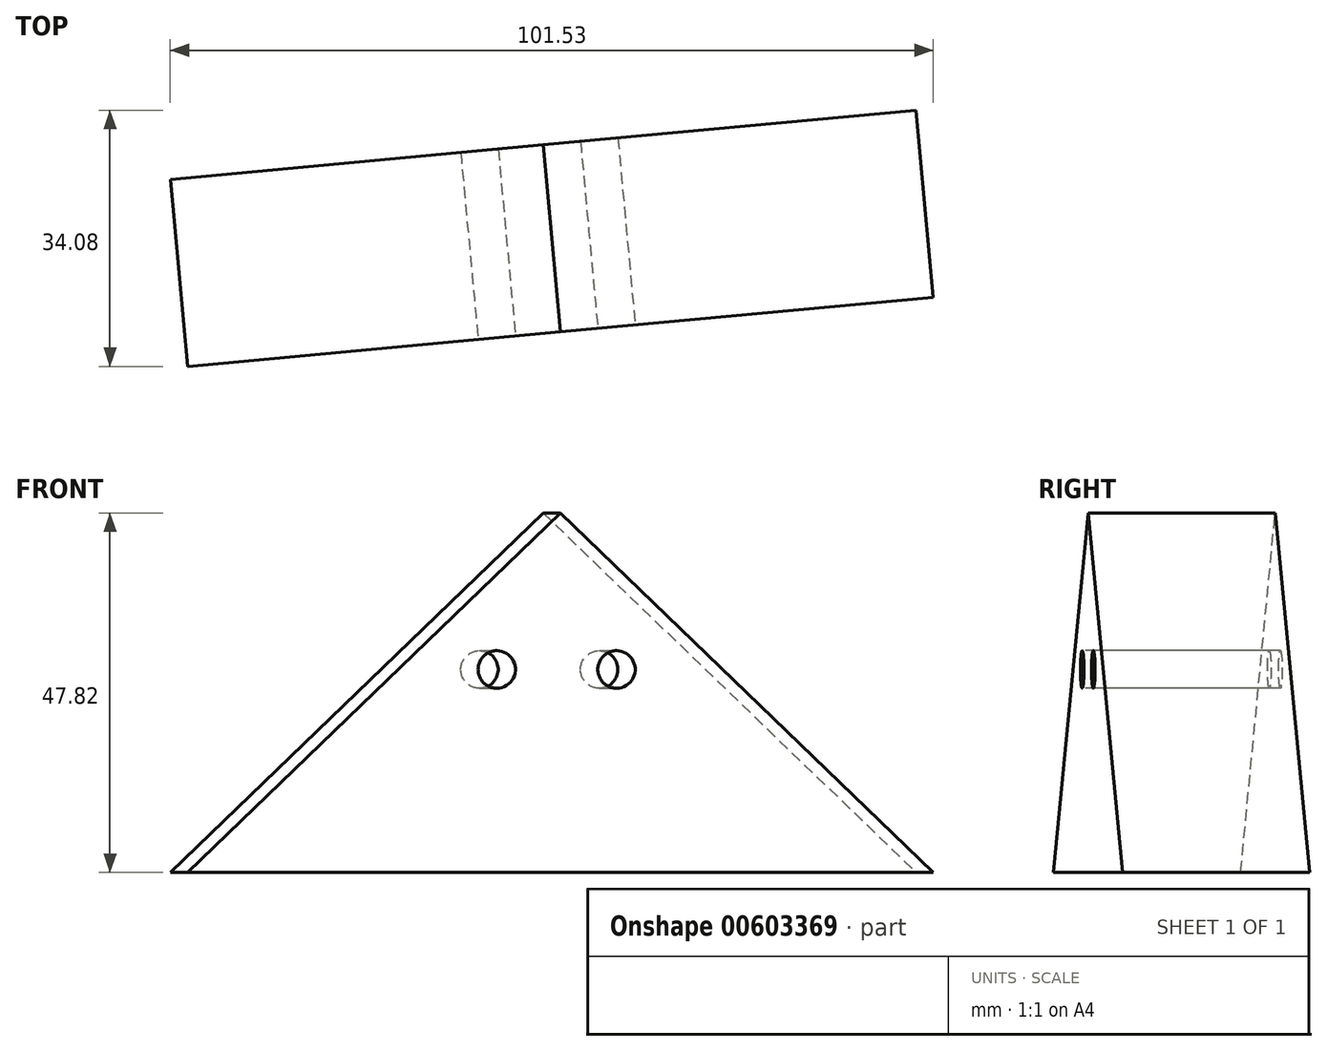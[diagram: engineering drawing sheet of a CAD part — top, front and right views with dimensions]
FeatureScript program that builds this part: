
annotation { "Feature Type Name" : "Feature", "Feature Type Description" : "" }
export const myFeature = defineFeature(function(context is Context, id is Id, definition is map)
    precondition{}
    {
        {
            var Q0;
            Q0=qCreatedBy(makeId("Top.planeOp"),FACE);
            var sketch = newSketch(context, id + "F0", { "sketchPlane" : qUnion([Q0])});
            skLineSegment(sketch, "E0", {"start": v(-327.3, -140.86) * mm, "end": v(-102.6, -140.86) * mm});
            skLineSegment(sketch, "E1", {"start": v(-102.6, -140.86) * mm, "end": v(-102.6, -170.86) * mm});
            skLineSegment(sketch, "E2", {"start": v(-102.6, -170.86) * mm, "end": v(0, -170.86) * mm});
            skLineSegment(sketch, "E3", {"start": v(0, -170.86) * mm, "end": v(0, -140.86) * mm});
            skLineSegment(sketch, "E4", {"start": v(0, -140.86) * mm, "end": v(288.9, -140.86) * mm});
            skLineSegment(sketch, "E5", {"start": v(288.9, -140.86) * mm, "end": v(288.9, 108.14) * mm});
            skLineSegment(sketch, "E6", {"start": v(288.9, 108.14) * mm, "end": v(0, 108.14) * mm});
            skLineSegment(sketch, "E7", {"start": v(0, 108.14) * mm, "end": v(0, 138.14) * mm});
            skLineSegment(sketch, "E8", {"start": v(-102.6, 128.64) * mm, "end": v(-102.6, 108.14) * mm});
            skLineSegment(sketch, "E9", {"start": v(-102.6, 108.14) * mm, "end": v(-327.3, 108.14) * mm});
            skLineSegment(sketch, "E10", {"start": v(-327.3, 108.14) * mm, "end": v(-327.3, -140.86) * mm});
            skLineSegment(sketch, "E11", {"start": v(-102.6, 128.64) * mm, "end": v(0, 138.14) * mm});
            skSolve(sketch);
        }
        {
            var Q0;
            Q0=makeQuery(id+"F0.imprint","IMPRINT",FACE,{"disambiguationData":[TD([[makeQuery(id+"F0.imprint","IMPRINT",EDGE,{"derivedFrom":sQuery(id+"F0.wireOp",EDGE,"E0")}),1.0]])]});
            extrude(context, id + "F1", {"entities" : qUnion([Q0]), "depth" : 8 * mm, "offsetDistance" : 25 * mm});
        }
        {
            var Q0;
            Q0=makeQuery(id+"F1.opExtrude","SWEPT_FACE",FACE,{"disambiguationData":[OSD([sQuery(id+"F0.wireOp",EDGE,"E5")])]});
            var sketch = newSketch(context, id + "F2", { "sketchPlane" : qUnion([Q0])});
            skLineSegment(sketch, "E12", {"start": v(-146.36, 8) * mm, "end": v(113.64, 8) * mm});
            skPoint(sketch, "E13", {"position": v(-140.86, 8) * mm});
            skPoint(sketch, "E14", {"position": v(108.14, 8) * mm});
            skLineSegment(sketch, "E15", {"start": v(-146.36, 8) * mm, "end": v(-16.36, 51.45) * mm});
            skLineSegment(sketch, "E16", {"start": v(-16.36, 51.45) * mm, "end": v(113.64, 8) * mm});
            skPoint(sketch, "E17", {"position": v(-16.36, 8) * mm});
            skSolve(sketch);
        }
        {
            var Q0;
            {var subQ0=sQuery(id+"F2.wireOp",EDGE,"E15");Q0=makeQuery(id+"F2.imprint","IMPRINT",FACE,{"disambiguationData":[TD([[makeQuery(id+"F2.imprint","IMPRINT",EDGE,{"derivedFrom":subQ0}),-1.0]])]});}
            extrude(context, id + "F3", {"entities" : qUnion([Q0]), "operationType" : NewBodyOperationType.ADD, "oppositeDirection" : true, "depth" : (616.2 + 5.5) * mm, "offsetDistance" : 25 * mm});
        }
        {
            var Q0;
            Q0=qSketchRegion(id+"F2",true);
            extrude(context, id + "F4", {"entities" : qUnion([Q0]), "operationType" : NewBodyOperationType.ADD, "depth" : 5.5 * mm, "offsetDistance" : 25 * mm});
        }
        {
            var Q0;
            Q0=makeQuery(id+"F1.opExtrude","SWEPT_FACE",FACE,{"disambiguationData":[OSD([sQuery(id+"F0.wireOp",EDGE,"E2")])]});
            var sketch = newSketch(context, id + "F5", { "sketchPlane" : qUnion([Q0])});
            skLineSegment(sketch, "E18", {"start": v(-108.1, 8) * mm, "end": v(5.5, 8) * mm});
            skPoint(sketch, "E19", {"position": v(-102.6, 8) * mm});
            skPoint(sketch, "E20", {"position": v(0, 8) * mm});
            skPoint(sketch, "E21", {"position": v(-51.3, 8) * mm});
            skLineSegment(sketch, "E22", {"start": v(-51.3, 8) * mm, "end": v(-51.3, 90.85) * mm, "construction": true});
            skPoint(sketch, "E23", {"position": v(-51.3, 62.75) * mm});
            skLineSegment(sketch, "E24", {"start": v(-108.1, 8) * mm, "end": v(-51.3, 62.75) * mm});
            skLineSegment(sketch, "E25", {"start": v(-51.3, 62.75) * mm, "end": v(5.5, 8) * mm});
            skSolve(sketch);
        }
        {
            var Q0;
            Q0=qSketchRegion(id+"F5",true);
            var Q1;
            Q1=makeQuery(id+"F1.opExtrude","SWEPT_FACE",FACE,{"disambiguationData":[OSD([sQuery(id+"F0.wireOp",EDGE,"E11")])]});
            extrude(context, id + "F6", {"entities" : qUnion([Q0]), "operationType" : NewBodyOperationType.ADD, "endBound" : BoundingType.UP_TO_SURFACE, "oppositeDirection" : true, "depth" : 25 * mm, "endBoundEntityFace" : qUnion([Q1]), "hasOffset" : true, "offsetDistance" : -5.5 * mm});
        }
        {
            var Q0;
            Q0=qSketchRegion(id+"F5",true);
            extrude(context, id + "F7", {"entities" : qUnion([Q0]), "operationType" : NewBodyOperationType.ADD, "depth" : 5.5 * mm, "offsetDistance" : 25 * mm});
        }
        {
            var Q0;
            Q0=makeQuery(id+"F6.opExtrude","CAP_FACE",FACE,{"disambiguationData":[OSD([sQuery(id+"F5.wireOp",EDGE,"E18"),sQuery(id+"F5.wireOp",EDGE,"E24"),sQuery(id+"F5.wireOp",EDGE,"E25")])],"isStart":false});
            var sketch = newSketch(context, id + "F8", { "sketchPlane" : qUnion([Q0])});
            skLineSegment(sketch, "E26.0", {"start": v(38.28, 55.82) * mm, "end": v(-15.3, 4.4) * mm});
            skLineSegment(sketch, "E26.1", {"start": v(91.86, 4.4) * mm, "end": v(38.28, 55.82) * mm});
            skLineSegment(sketch, "E27", {"start": v(-15.3, 4.4) * mm, "end": v(91.86, 4.4) * mm});
            skSolve(sketch);
        }
        {
            var Q0;
            {var subQ0=sQuery(id+"F8.wireOp",EDGE,"E26.1");var subQ1=sQuery(id+"F8.wireOp",EDGE,"E26.0");var subQ2=makeQuery(id+"F8.imprint","INTERSECT",VERTEX,{"derivedFrom":[subQ1,subQ0]});Q0=makeQuery(id+"F8.imprint","IMPRINT",FACE,{"disambiguationData":[TD([[makeQuery(id+"F8.imprint","IMPRINT",EDGE,{"disambiguationData":[TD([[subQ2,-1.0]])],"derivedFrom":subQ1}),1.0]])]});}
            extrude(context, id + "F9", {"entities" : qUnion([Q0]), "operationType" : NewBodyOperationType.REMOVE, "oppositeDirection" : true, "depth" : 5.5 * mm, "offsetDistance" : 25 * mm});
        }
        {
            var Q0;
            Q0=makeQuery(id+"F3.opExtrude","CAP_FACE",FACE,{"disambiguationData":[OSD([sQuery(id+"F2.wireOp",EDGE,"E12"),sQuery(id+"F2.wireOp",EDGE,"E15"),sQuery(id+"F2.wireOp",EDGE,"E16")])],"isStart":false});
            var sketch = newSketch(context, id + "F10", { "sketchPlane" : qUnion([Q0])});
            skLineSegment(sketch, "E28.0", {"start": v(16.36, 45.65) * mm, "end": v(-111.9, 2.78) * mm});
            skLineSegment(sketch, "E28.1", {"start": v(144.61, 2.78) * mm, "end": v(16.36, 45.65) * mm});
            skLineSegment(sketch, "E29", {"start": v(-111.9, 2.78) * mm, "end": v(144.61, 2.78) * mm});
            skSolve(sketch);
        }
        {
            var Q0;
            Q0=qSketchRegion(id+"F10",true);
            extrude(context, id + "F11", {"entities" : qUnion([Q0]), "operationType" : NewBodyOperationType.REMOVE, "oppositeDirection" : true, "depth" : 5.5 * mm, "offsetDistance" : 25 * mm});
        }
        {
            var Q0;
            Q0=makeQuery(id+"F4.opExtrude","CAP_FACE",FACE,{"disambiguationData":[OSD([sQuery(id+"F2.wireOp",EDGE,"E12"),sQuery(id+"F2.wireOp",EDGE,"E15"),sQuery(id+"F2.wireOp",EDGE,"E16")])],"isStart":false});
            var sketch = newSketch(context, id + "F12", { "sketchPlane" : qUnion([Q0])});
            skLineSegment(sketch, "E30.0", {"start": v(-16.36, 45.65) * mm, "end": v(111.9, 2.78) * mm});
            skLineSegment(sketch, "E30.1", {"start": v(-144.61, 2.78) * mm, "end": v(-16.36, 45.65) * mm});
            skLineSegment(sketch, "E31", {"start": v(-144.61, 2.78) * mm, "end": v(111.9, 2.78) * mm});
            skSolve(sketch);
        }
        {
            var Q0;
            Q0=qSketchRegion(id+"F12",true);
            extrude(context, id + "F13", {"entities" : qUnion([Q0]), "operationType" : NewBodyOperationType.REMOVE, "oppositeDirection" : true, "depth" : 5.5 * mm, "offsetDistance" : 25 * mm});
        }
        {
            var Q0;
            Q0=makeQuery(id+"F7.opExtrude","CAP_FACE",FACE,{"disambiguationData":[OSD([sQuery(id+"F5.wireOp",EDGE,"E18"),sQuery(id+"F5.wireOp",EDGE,"E24"),sQuery(id+"F5.wireOp",EDGE,"E25")])],"isStart":false});
            var sketch = newSketch(context, id + "F14", { "sketchPlane" : qUnion([Q0])});
            skLineSegment(sketch, "E32.0", {"start": v(-51.3, 55.11) * mm, "end": v(1.68, 4.04) * mm});
            skLineSegment(sketch, "E32.1", {"start": v(-104.28, 4.04) * mm, "end": v(-51.3, 55.11) * mm});
            skLineSegment(sketch, "E33", {"start": v(-104.28, 4.04) * mm, "end": v(1.68, 4.04) * mm});
            skSolve(sketch);
        }
        {
            var Q0;
            Q0=qSketchRegion(id+"F14",true);
            extrude(context, id + "F15", {"entities" : qUnion([Q0]), "operationType" : NewBodyOperationType.REMOVE, "oppositeDirection" : true, "depth" : 5.5 * mm, "offsetDistance" : 25 * mm});
        }
        {
            var Q0;
            Q0=makeQuery(id+"F4.opExtrude","CAP_FACE",FACE,{"disambiguationData":[OSD([sQuery(id+"F2.wireOp",EDGE,"E12"),sQuery(id+"F2.wireOp",EDGE,"E15"),sQuery(id+"F2.wireOp",EDGE,"E16")])],"isStart":false});
            var sketch = newSketch(context, id + "F16", { "sketchPlane" : qUnion([Q0])});
            skLineSegment(sketch, "E34", {"start": v(-36.64, 44.67) * mm, "end": v(-16.36, 51.45) * mm});
            skLineSegment(sketch, "E35", {"start": v(-16.36, 51.45) * mm, "end": v(3.93, 44.67) * mm});
            skLineSegment(sketch, "E36.0", {"start": v(-16.36, 55.67) * mm, "end": v(5.2, 48.47) * mm});
            skLineSegment(sketch, "E36.1", {"start": v(-37.91, 48.47) * mm, "end": v(-16.36, 55.67) * mm});
            skLineSegment(sketch, "E37", {"start": v(-37.91, 48.47) * mm, "end": v(-36.64, 44.67) * mm});
            skLineSegment(sketch, "E38", {"start": v(5.2, 48.47) * mm, "end": v(3.93, 44.67) * mm});
            skSolve(sketch);
        }
        {
            var Q0;
            Q0=makeQuery(id+"F16.imprint","IMPRINT",FACE,{"disambiguationData":[TD([[makeQuery(id+"F16.imprint","IMPRINT",EDGE,{"derivedFrom":sQuery(id+"F16.wireOp",EDGE,"E34")}),1.0]])]});
            extrude(context, id + "F17", {"entities" : qUnion([Q0]), "operationType" : NewBodyOperationType.ADD, "oppositeDirection" : true, "depth" : (30.35 + 277.85) * mm, "offsetDistance" : 25 * mm});
        }
        {
            var Q0;
            Q0=qSketchRegion(id+"F16",true);
            extrude(context, id + "F18", {"entities" : qUnion([Q0]), "operationType" : NewBodyOperationType.REMOVE, "oppositeDirection" : true, "depth" : 24 * mm, "offsetDistance" : 25 * mm});
        }
        {
            var Q0;
            Q0=makeQuery(id+"F3.opExtrude","CAP_FACE",FACE,{"disambiguationData":[OSD([sQuery(id+"F2.wireOp",EDGE,"E12"),sQuery(id+"F2.wireOp",EDGE,"E15"),sQuery(id+"F2.wireOp",EDGE,"E16")])],"isStart":false});
            var sketch = newSketch(context, id + "F19", { "sketchPlane" : qUnion([Q0])});
            skLineSegment(sketch, "E39", {"start": v(-3.93, 44.67) * mm, "end": v(16.36, 51.45) * mm});
            skLineSegment(sketch, "E40", {"start": v(16.36, 51.45) * mm, "end": v(36.64, 44.67) * mm});
            skLineSegment(sketch, "E41.0", {"start": v(16.36, 55.67) * mm, "end": v(37.91, 48.47) * mm});
            skLineSegment(sketch, "E41.1", {"start": v(-5.2, 48.47) * mm, "end": v(16.36, 55.67) * mm});
            skLineSegment(sketch, "E42", {"start": v(-5.2, 48.47) * mm, "end": v(-3.93, 44.67) * mm});
            skLineSegment(sketch, "E43", {"start": v(37.91, 48.47) * mm, "end": v(36.64, 44.67) * mm});
            skSolve(sketch);
        }
        {
            var Q0;
            Q0=qSketchRegion(id+"F19",true);
            extrude(context, id + "F20", {"entities" : qUnion([Q0]), "operationType" : NewBodyOperationType.ADD, "oppositeDirection" : true, "depth" : (30.35 + 213.85) * mm, "offsetDistance" : 25 * mm});
        }
        {
            var Q0;
            Q0=qSketchRegion(id+"F19",true);
            extrude(context, id + "F21", {"entities" : qUnion([Q0]), "operationType" : NewBodyOperationType.REMOVE, "oppositeDirection" : true, "depth" : 30.35 * mm, "offsetDistance" : 25 * mm});
        }
        {
            var Q0;
            Q0=makeQuery(id+"F11.boolean.opBoolean","MERGE",FACE,{"derivedFrom":[makeQuery(id+"F1.opExtrude","SWEPT_FACE",FACE,{"disambiguationData":[OSD([sQuery(id+"F0.wireOp",EDGE,"E10")])]}),makeQuery(id+"F11.opExtrude","CAP_FACE",FACE,{"disambiguationData":[OSD([sQuery(id+"F10.wireOp",EDGE,"E28.0"),sQuery(id+"F10.wireOp",EDGE,"E28.1"),sQuery(id+"F10.wireOp",EDGE,"E29")])],"isStart":false})]});
            var sketch = newSketch(context, id + "F22", { "sketchPlane" : qUnion([Q0])});
            skPoint(sketch, "E44", {"position": v(16.36, 0) * mm});
            skLineSegment(sketch, "E45", {"start": v(16.36, 0) * mm, "end": v(16.36, 35) * mm, "construction": true});
            skLineSegment(sketch, "E46", {"start": v(-4.2, 35) * mm, "end": v(35.76, 35) * mm, "construction": true});
            skPoint(sketch, "E47", {"position": v(8.36, 35) * mm});
            skPoint(sketch, "E48", {"position": v(24.36, 35) * mm});
            skCircle(sketch, "E49", {"center": v(8.36, 35) * mm, "radius": 2.5 * mm});
            skCircle(sketch, "E50", {"center": v(24.36, 35) * mm, "radius": 2.5 * mm});
            skSolve(sketch);
        }
        {
            var Q0;
            Q0=qSketchRegion(id+"F22",true);
            extrude(context, id + "F23", {"entities" : qUnion([Q0]), "operationType" : NewBodyOperationType.REMOVE, "oppositeDirection" : true, "depth" : .5 * mm, "offsetDistance" : 25 * mm});
        }
        {
            var Q0;
            Q0=makeQuery(id+"F13.boolean.opBoolean","MERGE",FACE,{"derivedFrom":[makeQuery(id+"F3.boolean.opBoolean","MERGE",FACE,{"derivedFrom":[makeQuery(id+"F1.opExtrude","SWEPT_FACE",FACE,{"disambiguationData":[OSD([sQuery(id+"F0.wireOp",EDGE,"E5")])]}),makeQuery(id+"F3.opExtrude","CAP_FACE",FACE,{"disambiguationData":[OSD([sQuery(id+"F2.wireOp",EDGE,"E12"),sQuery(id+"F2.wireOp",EDGE,"E15"),sQuery(id+"F2.wireOp",EDGE,"E16")])],"isStart":true})]}),makeQuery(id+"F13.opExtrude","CAP_FACE",FACE,{"disambiguationData":[OSD([sQuery(id+"F12.wireOp",EDGE,"E30.0"),sQuery(id+"F12.wireOp",EDGE,"E30.1"),sQuery(id+"F12.wireOp",EDGE,"E31")])],"isStart":false})]});
            var sketch = newSketch(context, id + "F24", { "sketchPlane" : qUnion([Q0])});
            skPoint(sketch, "E51", {"position": v(-16.36, 0) * mm});
            skLineSegment(sketch, "E52", {"start": v(-16.36, 0) * mm, "end": v(-16.36, 35) * mm, "construction": true});
            skLineSegment(sketch, "E53", {"start": v(-48.45, 35) * mm, "end": v(-8.49, 35) * mm, "construction": true});
            skPoint(sketch, "E54", {"position": v(-24.36, 35) * mm});
            skPoint(sketch, "E55", {"position": v(-8.36, 35) * mm});
            skCircle(sketch, "E56", {"center": v(-24.36, 35) * mm, "radius": 2.5 * mm});
            skCircle(sketch, "E57", {"center": v(-8.36, 35) * mm, "radius": 2.5 * mm});
            skSolve(sketch);
        }
        {
            var Q0;
            Q0=qSketchRegion(id+"F24",true);
            extrude(context, id + "F25", {"entities" : qUnion([Q0]), "operationType" : NewBodyOperationType.REMOVE, "oppositeDirection" : true, "depth" : .5 * mm, "offsetDistance" : 25 * mm});
        }
        {
            var Q0;
            Q0=makeQuery(id+"F15.boolean.opBoolean","MERGE",FACE,{"derivedFrom":[makeQuery(id+"F6.boolean.opBoolean","MERGE",FACE,{"derivedFrom":[makeQuery(id+"F1.opExtrude","SWEPT_FACE",FACE,{"disambiguationData":[OSD([sQuery(id+"F0.wireOp",EDGE,"E2")])]}),makeQuery(id+"F6.opExtrude","CAP_FACE",FACE,{"disambiguationData":[OSD([sQuery(id+"F5.wireOp",EDGE,"E18"),sQuery(id+"F5.wireOp",EDGE,"E24"),sQuery(id+"F5.wireOp",EDGE,"E25")])],"isStart":true})]})],"fromTools":[makeQuery(id+"F15.opExtrude","CAP_FACE",FACE,{"disambiguationData":[OSD([sQuery(id+"F14.wireOp",EDGE,"E32.0"),sQuery(id+"F14.wireOp",EDGE,"E32.1"),sQuery(id+"F14.wireOp",EDGE,"E33")])],"isStart":false})]});
            var sketch = newSketch(context, id + "F26", { "sketchPlane" : qUnion([Q0])});
            skPoint(sketch, "E58", {"position": v(-51.3, 0) * mm});
            skLineSegment(sketch, "E59", {"start": v(-51.3, 0) * mm, "end": v(-51.3, 35) * mm, "construction": true});
            skLineSegment(sketch, "E60", {"start": v(-73.66, 35) * mm, "end": v(-33.7, 35) * mm, "construction": true});
            skPoint(sketch, "E61", {"position": v(-59.3, 35) * mm});
            skPoint(sketch, "E62", {"position": v(-43.3, 35) * mm});
            skCircle(sketch, "E63", {"center": v(-59.3, 35) * mm, "radius": 2.5 * mm});
            skCircle(sketch, "E64", {"center": v(-43.3, 35) * mm, "radius": 2.5 * mm});
            skSolve(sketch);
        }
        {
            var Q0;
            Q0=qSketchRegion(id+"F26",true);
            extrude(context, id + "F27", {"entities" : qUnion([Q0]), "operationType" : NewBodyOperationType.REMOVE, "oppositeDirection" : true, "depth" : .5 * mm, "offsetDistance" : 25 * mm});
        }
        {
            var Q0;
            Q0=makeQuery(id+"F1.opExtrude","SWEPT_FACE",FACE,{"disambiguationData":[OSD([sQuery(id+"F0.wireOp",EDGE,"E11")])]});
            var sketch = newSketch(context, id + "F28", { "sketchPlane" : qUnion([Q0])});
            skPoint(sketch, "E65", {"position": v(38.78, 0) * mm});
            skLineSegment(sketch, "E66", {"start": v(38.78, 0) * mm, "end": v(38.78, 35) * mm, "construction": true});
            skLineSegment(sketch, "E67", {"start": v(13.04, 35) * mm, "end": v(53, 35) * mm, "construction": true});
            skPoint(sketch, "E68", {"position": v(30.78, 35) * mm});
            skPoint(sketch, "E69", {"position": v(46.78, 35) * mm});
            skCircle(sketch, "E70", {"center": v(30.78, 35) * mm, "radius": 2.5 * mm});
            skCircle(sketch, "E71", {"center": v(46.78, 35) * mm, "radius": 2.5 * mm});
            skSolve(sketch);
        }
        {
            var Q0;
            Q0=qSketchRegion(id+"F28",true);
            extrude(context, id + "F29", {"entities" : qUnion([Q0]), "operationType" : NewBodyOperationType.REMOVE, "oppositeDirection" : true, "depth" : .5 * mm, "offsetDistance" : 25 * mm});
        }
        {
            var Q0;
            Q0=makeQuery(id+"F13.boolean.opBoolean","MERGE",FACE,{"derivedFrom":[makeQuery(id+"F3.boolean.opBoolean","MERGE",FACE,{"derivedFrom":[makeQuery(id+"F1.opExtrude","SWEPT_FACE",FACE,{"disambiguationData":[OSD([sQuery(id+"F0.wireOp",EDGE,"E5")])]}),makeQuery(id+"F3.opExtrude","CAP_FACE",FACE,{"disambiguationData":[OSD([sQuery(id+"F2.wireOp",EDGE,"E12"),sQuery(id+"F2.wireOp",EDGE,"E15"),sQuery(id+"F2.wireOp",EDGE,"E16")])],"isStart":true})]}),makeQuery(id+"F13.opExtrude","CAP_FACE",FACE,{"disambiguationData":[OSD([sQuery(id+"F12.wireOp",EDGE,"E30.0"),sQuery(id+"F12.wireOp",EDGE,"E30.1"),sQuery(id+"F12.wireOp",EDGE,"E31")])],"isStart":false})]});
            var sketch = newSketch(context, id + "F30", { "sketchPlane" : qUnion([Q0])});
            skPoint(sketch, "E72", {"position": v(-16.36, 0) * mm});
            skLineSegment(sketch, "E73", {"start": v(-16.36, 0) * mm, "end": v(-16.36, 40.85) * mm, "construction": true});
            skLineSegment(sketch, "E74.bottom", {"start": v(-23.43, 23) * mm, "end": v(-9.29, 23) * mm});
            skLineSegment(sketch, "E74.top", {"start": v(-23.43, 5) * mm, "end": v(-9.29, 5) * mm});
            skLineSegment(sketch, "E74.left", {"start": v(-23.43, 23) * mm, "end": v(-23.43, 5) * mm});
            skLineSegment(sketch, "E74.right", {"start": v(-9.29, 23) * mm, "end": v(-9.29, 5) * mm});
            skLineSegment(sketch, "E75.0", {"start": v(-21.5, 21.07) * mm, "end": v(-17.32, 21.07) * mm});
            skLineSegment(sketch, "E75.1", {"start": v(-21.5, 21.07) * mm, "end": v(-21.5, 14.96) * mm});
            skLineSegment(sketch, "E75.2", {"start": v(-21.5, 6.93) * mm, "end": v(-17.32, 6.93) * mm});
            skLineSegment(sketch, "E75.3", {"start": v(-11.21, 21.07) * mm, "end": v(-11.21, 14.96) * mm});
            skLineSegment(sketch, "E76.left", {"start": v(-17.32, 21.07) * mm, "end": v(-17.32, 14.96) * mm});
            skLineSegment(sketch, "E76.right", {"start": v(-15.4, 21.07) * mm, "end": v(-15.4, 14.96) * mm});
            skLineSegment(sketch, "E77.bottom", {"start": v(-11.21, 14.96) * mm, "end": v(-15.4, 14.96) * mm});
            skLineSegment(sketch, "E77.top", {"start": v(-11.21, 13.04) * mm, "end": v(-15.4, 13.04) * mm});
            skLineSegment(sketch, "E78.trimOffspring", {"start": v(-17.32, 14.96) * mm, "end": v(-21.5, 14.96) * mm});
            skLineSegment(sketch, "E79.trimOffspring", {"start": v(-17.32, 13.04) * mm, "end": v(-17.32, 6.93) * mm});
            skLineSegment(sketch, "E80.trimOffspring", {"start": v(-17.32, 13.04) * mm, "end": v(-21.5, 13.04) * mm});
            skLineSegment(sketch, "E81.trimOffspring", {"start": v(-15.4, 13.04) * mm, "end": v(-15.4, 6.93) * mm});
            skLineSegment(sketch, "E82.trimOffspring", {"start": v(-11.21, 13.04) * mm, "end": v(-11.21, 6.93) * mm});
            skLineSegment(sketch, "E83.trimOffspring", {"start": v(-21.5, 13.04) * mm, "end": v(-21.5, 6.93) * mm});
            skLineSegment(sketch, "E84.trimOffspring", {"start": v(-15.4, 21.07) * mm, "end": v(-11.21, 21.07) * mm});
            skLineSegment(sketch, "E85.trimOffspring", {"start": v(-15.4, 6.93) * mm, "end": v(-11.21, 6.93) * mm});
            skPoint(sketch, "E86", {"position": v(-16.36, 23) * mm});
            skLineSegment(sketch, "E87.1.0.0", {"start": v(19.6, 13.04) * mm, "end": v(19.6, 6.93) * mm});
            skPoint(sketch, "E87.1.0.1", {"position": v(18.64, 23) * mm});
            skLineSegment(sketch, "E87.1.0.2", {"start": v(19.6, 6.93) * mm, "end": v(23.79, 6.93) * mm});
            skLineSegment(sketch, "E87.1.0.3", {"start": v(13.5, 13.04) * mm, "end": v(13.5, 6.93) * mm});
            skLineSegment(sketch, "E87.1.0.4", {"start": v(17.68, 13.04) * mm, "end": v(17.68, 6.93) * mm});
            skLineSegment(sketch, "E87.1.0.5", {"start": v(11.57, 5) * mm, "end": v(25.71, 5) * mm});
            skLineSegment(sketch, "E87.1.0.6", {"start": v(11.57, 23) * mm, "end": v(25.71, 23) * mm});
            skLineSegment(sketch, "E87.1.0.7", {"start": v(25.71, 23) * mm, "end": v(25.71, 5) * mm});
            skLineSegment(sketch, "E87.1.0.8", {"start": v(11.57, 23) * mm, "end": v(11.57, 5) * mm});
            skLineSegment(sketch, "E87.1.0.9", {"start": v(23.79, 13.04) * mm, "end": v(23.79, 6.93) * mm});
            skLineSegment(sketch, "E87.1.0.10", {"start": v(23.79, 13.04) * mm, "end": v(19.6, 13.04) * mm});
            skLineSegment(sketch, "E87.1.0.11", {"start": v(17.68, 21.07) * mm, "end": v(17.68, 14.96) * mm});
            skLineSegment(sketch, "E87.1.0.12", {"start": v(13.5, 21.07) * mm, "end": v(17.68, 21.07) * mm});
            skLineSegment(sketch, "E87.1.0.13", {"start": v(19.6, 21.07) * mm, "end": v(19.6, 14.96) * mm});
            skLineSegment(sketch, "E87.1.0.14", {"start": v(13.5, 6.93) * mm, "end": v(17.68, 6.93) * mm});
            skLineSegment(sketch, "E87.1.0.15", {"start": v(23.79, 21.07) * mm, "end": v(23.79, 14.96) * mm});
            skLineSegment(sketch, "E87.1.0.16", {"start": v(17.68, 13.04) * mm, "end": v(13.5, 13.04) * mm});
            skLineSegment(sketch, "E87.1.0.17", {"start": v(17.68, 14.96) * mm, "end": v(13.5, 14.96) * mm});
            skLineSegment(sketch, "E87.1.0.18", {"start": v(23.79, 14.96) * mm, "end": v(19.6, 14.96) * mm});
            skLineSegment(sketch, "E87.1.0.19", {"start": v(19.6, 21.07) * mm, "end": v(23.79, 21.07) * mm});
            skLineSegment(sketch, "E87.1.0.20", {"start": v(13.5, 21.07) * mm, "end": v(13.5, 14.96) * mm});
            skLineSegment(sketch, "E87.direction1", {"start": v(-23.43, 5) * mm, "end": v(11.57, 5) * mm, "construction": true});
            skLineSegment(sketch, "E88.1.0.0", {"start": v(-50.4, 6.93) * mm, "end": v(-46.21, 6.93) * mm});
            skPoint(sketch, "E88.1.0.1", {"position": v(-51.36, 0) * mm});
            skLineSegment(sketch, "E88.1.0.2", {"start": v(-58.43, 5) * mm, "end": v(-44.29, 5) * mm});
            skLineSegment(sketch, "E88.1.0.3", {"start": v(-44.29, 23) * mm, "end": v(-44.29, 5) * mm});
            skLineSegment(sketch, "E88.1.0.4", {"start": v(-58.43, 23) * mm, "end": v(-58.43, 5) * mm});
            skLineSegment(sketch, "E88.1.0.5", {"start": v(-46.21, 21.07) * mm, "end": v(-46.21, 14.96) * mm});
            skLineSegment(sketch, "E88.1.0.6", {"start": v(-56.5, 6.93) * mm, "end": v(-52.32, 6.93) * mm});
            skPoint(sketch, "E88.1.0.7", {"position": v(-51.36, 23) * mm});
            skLineSegment(sketch, "E88.1.0.8", {"start": v(-50.4, 13.04) * mm, "end": v(-50.4, 6.93) * mm});
            skLineSegment(sketch, "E88.1.0.9", {"start": v(-52.32, 13.04) * mm, "end": v(-56.5, 13.04) * mm});
            skLineSegment(sketch, "E88.1.0.10", {"start": v(-52.32, 13.04) * mm, "end": v(-52.32, 6.93) * mm});
            skLineSegment(sketch, "E88.1.0.11", {"start": v(-58.43, 23) * mm, "end": v(-44.29, 23) * mm});
            skLineSegment(sketch, "E88.1.0.12", {"start": v(-52.32, 14.96) * mm, "end": v(-56.5, 14.96) * mm});
            skLineSegment(sketch, "E88.1.0.13", {"start": v(-46.21, 13.04) * mm, "end": v(-50.4, 13.04) * mm});
            skLineSegment(sketch, "E88.1.0.14", {"start": v(-46.21, 14.96) * mm, "end": v(-50.4, 14.96) * mm});
            skLineSegment(sketch, "E88.1.0.15", {"start": v(-50.4, 21.07) * mm, "end": v(-46.21, 21.07) * mm});
            skLineSegment(sketch, "E88.1.0.16", {"start": v(-56.5, 21.07) * mm, "end": v(-56.5, 14.96) * mm});
            skLineSegment(sketch, "E88.1.0.17", {"start": v(-56.5, 21.07) * mm, "end": v(-52.32, 21.07) * mm});
            skLineSegment(sketch, "E88.1.0.18", {"start": v(-50.4, 21.07) * mm, "end": v(-50.4, 14.96) * mm});
            skLineSegment(sketch, "E88.1.0.19", {"start": v(-52.32, 21.07) * mm, "end": v(-52.32, 14.96) * mm});
            skLineSegment(sketch, "E88.1.0.20", {"start": v(-56.5, 13.04) * mm, "end": v(-56.5, 6.93) * mm});
            skLineSegment(sketch, "E88.1.0.21", {"start": v(-46.21, 13.04) * mm, "end": v(-46.21, 6.93) * mm});
            skLineSegment(sketch, "E88.direction1", {"start": v(-23.43, 5) * mm, "end": v(-58.43, 5) * mm, "construction": true});
            skSolve(sketch);
        }
        {
            var Q0;
            Q0=qSketchRegion(id+"F30",true);
            extrude(context, id + "F31", {"entities" : qUnion([Q0]), "operationType" : NewBodyOperationType.REMOVE, "oppositeDirection" : true, "depth" : 0.5 * mm, "offsetDistance" : 25 * mm});
        }
        {
            var Q0;
            Q0=makeQuery(id+"F9.boolean.opBoolean","COPY",FACE,{"derivedFrom":makeQuery(id+"F9.opExtrude","CAP_FACE",FACE,{"disambiguationData":[OSD([sQuery(id+"F0.wireOp",EDGE,"E11"),sQuery(id+"F5.wireOp",EDGE,"E18"),sQuery(id+"F8.wireOp",EDGE,"E26.0"),sQuery(id+"F8.wireOp",EDGE,"E26.1")])],"isStart":false})});
            extrude(context, id + "F32", {"entities" : qUnion([Q0]), "depth" : 25 * mm, "offsetDistance" : 25 * mm});
        }
        {
            var Q0;
            Q0=makeQuery(id+"F1.opExtrude","SWEPT_BODY",BODY,{"disambiguationData":[OSD([sQuery(id+"F0.wireOp",EDGE,"E0"),sQuery(id+"F0.wireOp",EDGE,"E1"),sQuery(id+"F0.wireOp",EDGE,"E2"),sQuery(id+"F0.wireOp",EDGE,"E3"),sQuery(id+"F0.wireOp",EDGE,"E4"),sQuery(id+"F0.wireOp",EDGE,"E5"),sQuery(id+"F0.wireOp",EDGE,"E6"),sQuery(id+"F0.wireOp",EDGE,"E7"),sQuery(id+"F0.wireOp",EDGE,"E8"),sQuery(id+"F0.wireOp",EDGE,"E9"),sQuery(id+"F0.wireOp",EDGE,"E10"),sQuery(id+"F0.wireOp",EDGE,"E11")])]});
            deleteBodies(context, id + "F33", {"entities" : qUnion([Q0])});
        }
    });
